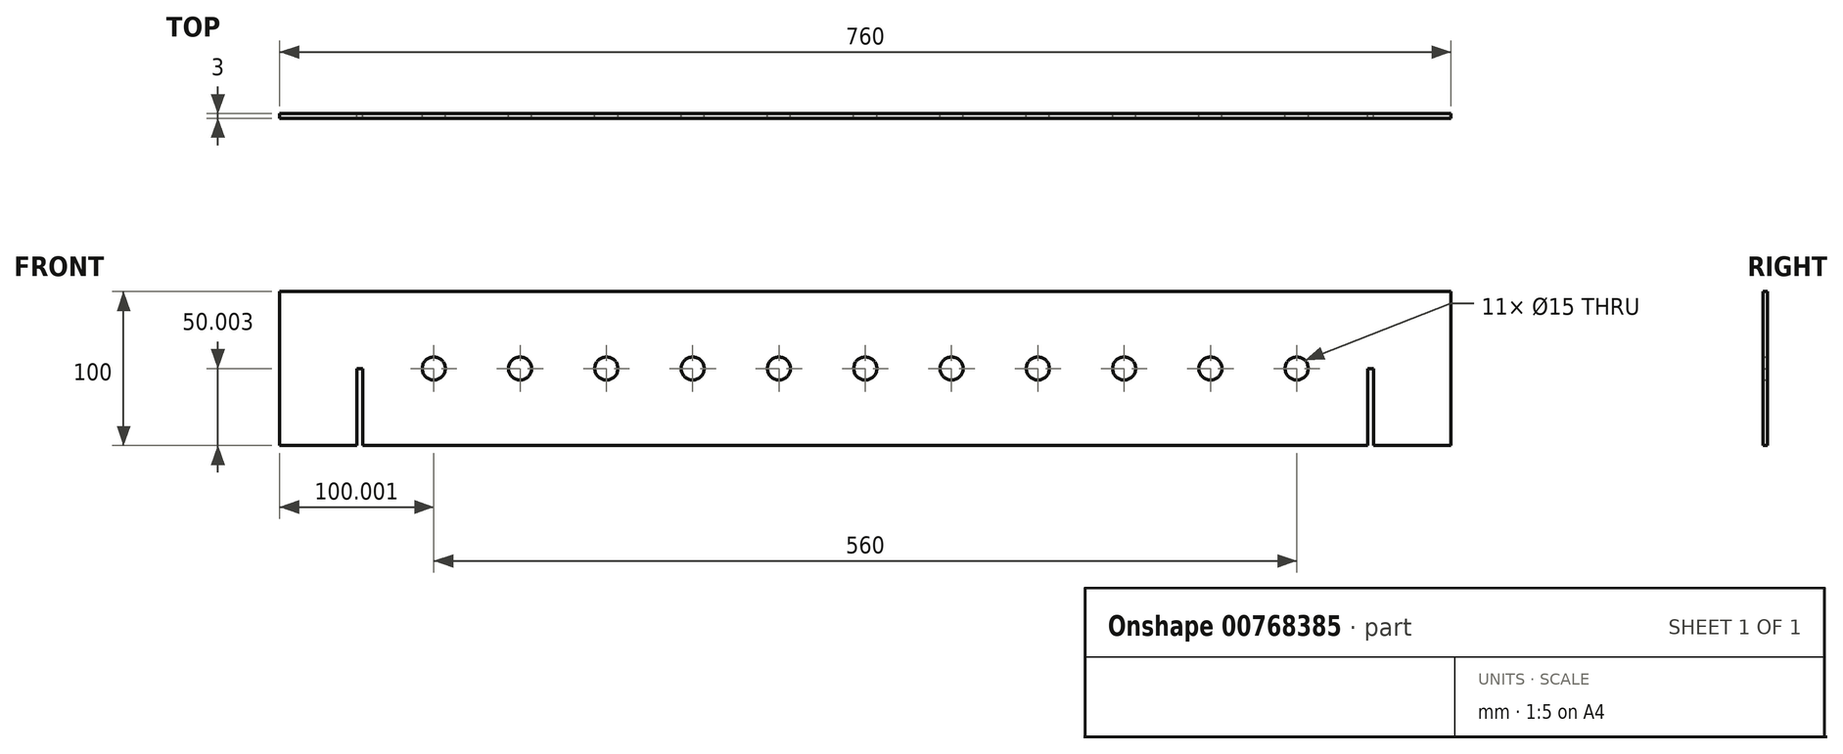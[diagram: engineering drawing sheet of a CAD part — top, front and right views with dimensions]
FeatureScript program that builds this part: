
annotation { "Feature Type Name" : "Feature", "Feature Type Description" : "" }
export const myFeature = defineFeature(function(context is Context, id is Id, definition is map)
    precondition{}
    {
        {
            var Q0;
            Q0=qCreatedBy(makeId("Front.planeOp"),FACE);
            var sketch = newSketch(context, id + "F0", { "sketchPlane" : qUnion([Q0])});
            skLineSegment(sketch, "E0.bottom", {"start": v(-271.9, -40.23) * mm, "end": v(488.1, -40.23) * mm});
            skLineSegment(sketch, "E0.top", {"start": v(-271.9, -140.23) * mm, "end": v(488.1, -140.23) * mm});
            skLineSegment(sketch, "E0.left", {"start": v(-271.9, -40.23) * mm, "end": v(-271.9, -140.23) * mm});
            skLineSegment(sketch, "E0.right", {"start": v(488.1, -40.23) * mm, "end": v(488.1, -140.23) * mm});
            skLineSegment(sketch, "E1.bottom", {"start": v(-221.9, -90.23) * mm, "end": v(-217.9, -90.23) * mm});
            skLineSegment(sketch, "E1.top", {"start": v(-221.9, -140.23) * mm, "end": v(-217.9, -140.23) * mm});
            skLineSegment(sketch, "E1.left", {"start": v(-221.9, -90.23) * mm, "end": v(-221.9, -140.23) * mm});
            skLineSegment(sketch, "E1.right", {"start": v(-217.9, -90.23) * mm, "end": v(-217.9, -140.23) * mm});
            skLineSegment(sketch, "E2.bottom", {"start": v(434.1, -90.23) * mm, "end": v(438.1, -90.23) * mm});
            skLineSegment(sketch, "E2.top", {"start": v(434.1, -140.23) * mm, "end": v(438.1, -140.23) * mm});
            skLineSegment(sketch, "E2.left", {"start": v(434.1, -90.23) * mm, "end": v(434.1, -140.23) * mm});
            skLineSegment(sketch, "E2.right", {"start": v(438.1, -90.23) * mm, "end": v(438.1, -140.23) * mm});
            skLineSegment(sketch, "E3", {"start": v(-271.9, -90.23) * mm, "end": v(488.1, -90.23) * mm, "construction": true});
            skCircle(sketch, "E4", {"center": v(-171.9, -90.23) * mm, "radius": 7.5 * mm});
            skCircle(sketch, "E5.1.0.0", {"center": v(-115.9, -90.23) * mm, "radius": 7.5 * mm});
            skCircle(sketch, "E5.2.0.0", {"center": v(-59.9, -90.23) * mm, "radius": 7.5 * mm});
            skCircle(sketch, "E5.3.0.0", {"center": v(-3.9, -90.23) * mm, "radius": 7.5 * mm});
            skCircle(sketch, "E5.4.0.0", {"center": v(52.1, -90.23) * mm, "radius": 7.5 * mm});
            skCircle(sketch, "E5.5.0.0", {"center": v(108.1, -90.23) * mm, "radius": 7.5 * mm});
            skCircle(sketch, "E5.6.0.0", {"center": v(164.1, -90.23) * mm, "radius": 7.5 * mm});
            skCircle(sketch, "E5.7.0.0", {"center": v(220.1, -90.23) * mm, "radius": 7.5 * mm});
            skCircle(sketch, "E5.8.0.0", {"center": v(276.1, -90.23) * mm, "radius": 7.5 * mm});
            skCircle(sketch, "E5.9.0.0", {"center": v(332.1, -90.23) * mm, "radius": 7.5 * mm});
            skCircle(sketch, "E5.10.0.0", {"center": v(388.1, -90.23) * mm, "radius": 7.5 * mm});
            skLineSegment(sketch, "E5.direction1", {"start": v(-171.9, -90.23) * mm, "end": v(-115.9, -90.23) * mm, "construction": true});
            skSolve(sketch);
        }
        {
            var Q0;
            Q0=makeQuery(id+"F0.imprint","IMPRINT",FACE,{"disambiguationData":[TD([[makeQuery(id+"F0.imprint","IMPRINT",EDGE,{"derivedFrom":sQuery(id+"F0.wireOp",EDGE,"E0.bottom")}),-1.0]])]});
            extrude(context, id + "F1", {"entities" : qUnion([Q0]), "depth" : 3 * mm, "offsetDistance" : 25 * mm});
        }
    });
